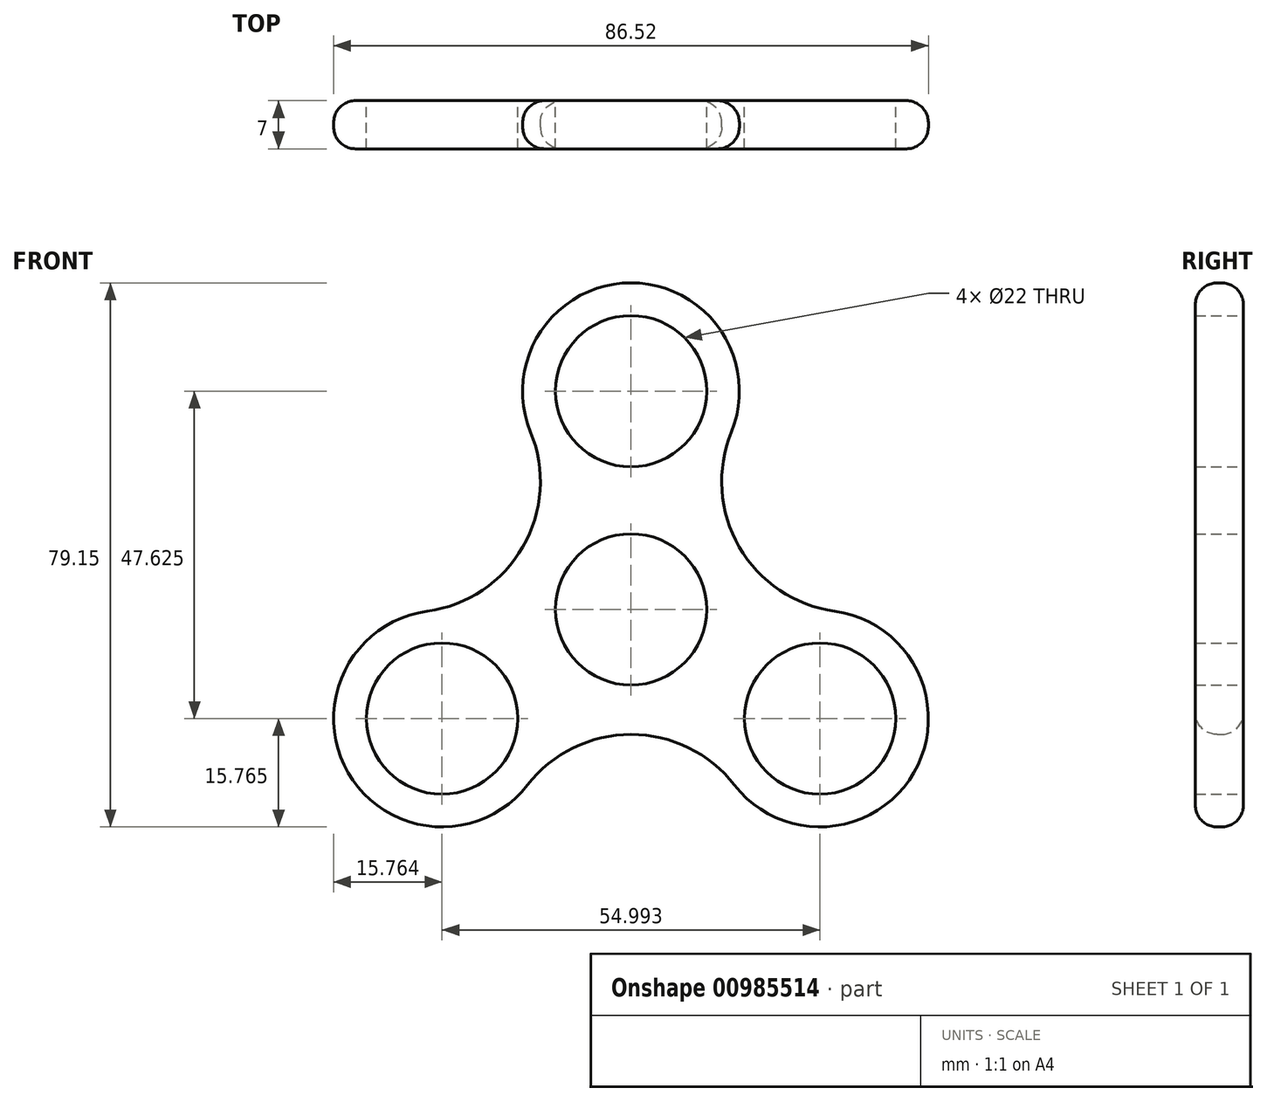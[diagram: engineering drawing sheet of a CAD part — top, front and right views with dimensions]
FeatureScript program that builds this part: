
annotation { "Feature Type Name" : "Feature", "Feature Type Description" : "" }
export const myFeature = defineFeature(function(context is Context, id is Id, definition is map)
    precondition{}
    {
        {
            var Q0;
            Q0=qCreatedBy(makeId("Front.planeOp"),FACE);
            var sketch = newSketch(context, id + "F0", { "sketchPlane" : qUnion([Q0])});
            skCircle(sketch, "E0", {"center": v(0, 0) * mm, "radius": 11 * mm});
            skCircle(sketch, "E1", {"center": v(0, 31.75) * mm, "radius": 11 * mm});
            skCircle(sketch, "E2", {"center": v(0, 31.75) * mm, "radius": 15.76 * mm});
            skCircle(sketch, "E3.1.0", {"center": v(-27.5, -15.87) * mm, "radius": 15.76 * mm});
            skCircle(sketch, "E3.1.1", {"center": v(-27.5, -15.87) * mm, "radius": 11 * mm});
            skCircle(sketch, "E3.2.0", {"center": v(27.5, -15.87) * mm, "radius": 15.76 * mm});
            skCircle(sketch, "E3.2.1", {"center": v(27.5, -15.87) * mm, "radius": 11 * mm});
            skArc(sketch, "E4", {"start": v(14.6, 25.8) * mm, "mid": v(15.74, 9.09) * mm, "end": v(29.64, -0.26) * mm});
            skPoint(sketch, "E4.first.point", {"position": v(14.6, 25.8) * mm});
            skPoint(sketch, "E4.second.point", {"position": v(29.64, -0.26) * mm});
            skArc(sketch, "E5.1.0", {"start": v(-29.64, -0.26) * mm, "mid": v(-15.74, 9.09) * mm, "end": v(-14.6, 25.8) * mm});
            skArc(sketch, "E5.2.0", {"start": v(15.05, -25.54) * mm, "mid": v(0, -18.18) * mm, "end": v(-15.05, -25.54) * mm});
            skSolve(sketch);
        }
        {
            var Q0;
            Q0 = qSketchRegion(id + "F0", true);
            extrude(context, id + "F1", {"entities" : qUnion([Q0]), "endBound" : BoundingType.SYMMETRIC, "depth" : 7 * mm, "offsetDistance" : 25 * mm});
        }
        {
            var Q0;
            Q0=makeQuery(id+"F1.opExtrude","CAP_EDGE",EDGE,{"disambiguationData":[OSD([sQuery(id+"F0.wireOp",EDGE,"E3.1.0")])],"isStart":false});
            var Q1;
            Q1=makeQuery(id+"F1.opExtrude","CAP_EDGE",EDGE,{"disambiguationData":[OSD([sQuery(id+"F0.wireOp",EDGE,"E3.1.0")])],"isStart":true});
            fillet(context, id + "F2", {"entities" : qUnion([Q0, Q1]), "radius" : 3.17 * mm, "tangentPropagation" : true, "allowEdgeOverflow" : false});
        }
    });
